# Revit family: dl_r__30_led___pl1_2s_5xa5132j1b08a5_5685
name_source: partatom
category: Lighting Fixtures
units: mm (PartAtom-declared; Revit-internal decimal feet)

## family parameters
Cut with Voids When Loaded = No
Host = Face
Light Source = No
Part Type = Normal
Room Calculation Point = No
Round Connector Dimension = Use Diameter
Shared = No

## types (1)
- --- (1 x LED, 5780 lm, 52 W, 3000K)
    Apparent Load = 52 VA
    CIE Flux Codes = 32 71 97 100 100
    Color Rendering = 80
    Color Temperature = 3000K
    Default Elevation = 1800 mm
    Description = DL® 30 LED, mast luminaire, primary light control with 3 zone facetted reflector, of plastic, silver coated, highly specular, primary optical cover: cover, of PMMA, structured, transparent, light distribution: PL1.2s, light emission: direct distribution, primary light characteristic: symmetric, installation type: post-top, LED, High Power LED, rated luminous flux: 5.780lm, luminous efficacy: 111lm/W, light colour: 830, colour temperature: 3000K, control gear: Plus, control: flexible luminous flux parameterisation, time-dependent luminous flux control, constant luminous flux control, digital communication interface, power reduction, electronic power reduction, mains connection: 230..240V, AC, 50/60Hz, start of lifetime: 52W, end of service life: 54W, reduction: 24W, luminaire housing, of diecast aluminium, powder-coated, Siteco® metallic grey (DB 702S), length: 600mm, width: 510mm, height: 290mm, spigot size: d x l = 76 x 100mm (post-top) | with reducer (optional accessory) 60 x 100mm, mounting height: 3..6m, protection rating (complete): IP66, insulation class (complete): insulation class II (safety insulation), certification: CE, ENEC, VDE, impact resistance: IK08, permissible operating ambient temperature: -25..+25°C, standard-compliant lighting for roads and squares, packaging unit: 1 piece

Light Distribution: PL1.2s
    Height = 290 mm
    Lamp = 1 x LED
    Lamp Light Flux = 5780 lm
    Lamp Power = 52 W
    Lamp count = 1
    Length = 510 mm
    Luminous efficacy = 111 lm/W
    Manufacturer = Siteco
    ModVariant = No
    Model = 5XA5132J1B08A5
    Number of Poles = 1
    OnlyDefault = Yes
    Power Factor = 1
    Product Name = DL® 30 LED | PL1.2s
    Product group = mast luminaire | pylon top
    ProductGroupID = 6100
    Protection Class = Protection class II
    Protection Degree = IP 66
    RLX_Detail_Level = 1
    RLX_Emergency_Light_Flux = 0 lm
    RLX_Emergency_Type = 0
    RLX_Emergency_Type_DB = No
    RlxData = <blob elided: 80961 chars, md5=32098f3d>
    Socket = socket
    Standby Power = 0 W
    System Light Flux = 5780 lm
    System Power = 52 W
    Type Comments = factory setting: luminous flux: 100 % | dim-lin: 254 | 526 mA
    Type Image = l_1006004.jpg
    URL = http://relux.com
    VarID = @adj_219009
    Voltage = 0 V
    Weight = 0.00 kg
    Width = 600 mm

## geometry (parser evidence)
native form markers: Sweep x11
no freeform markers — native parametric forms only
